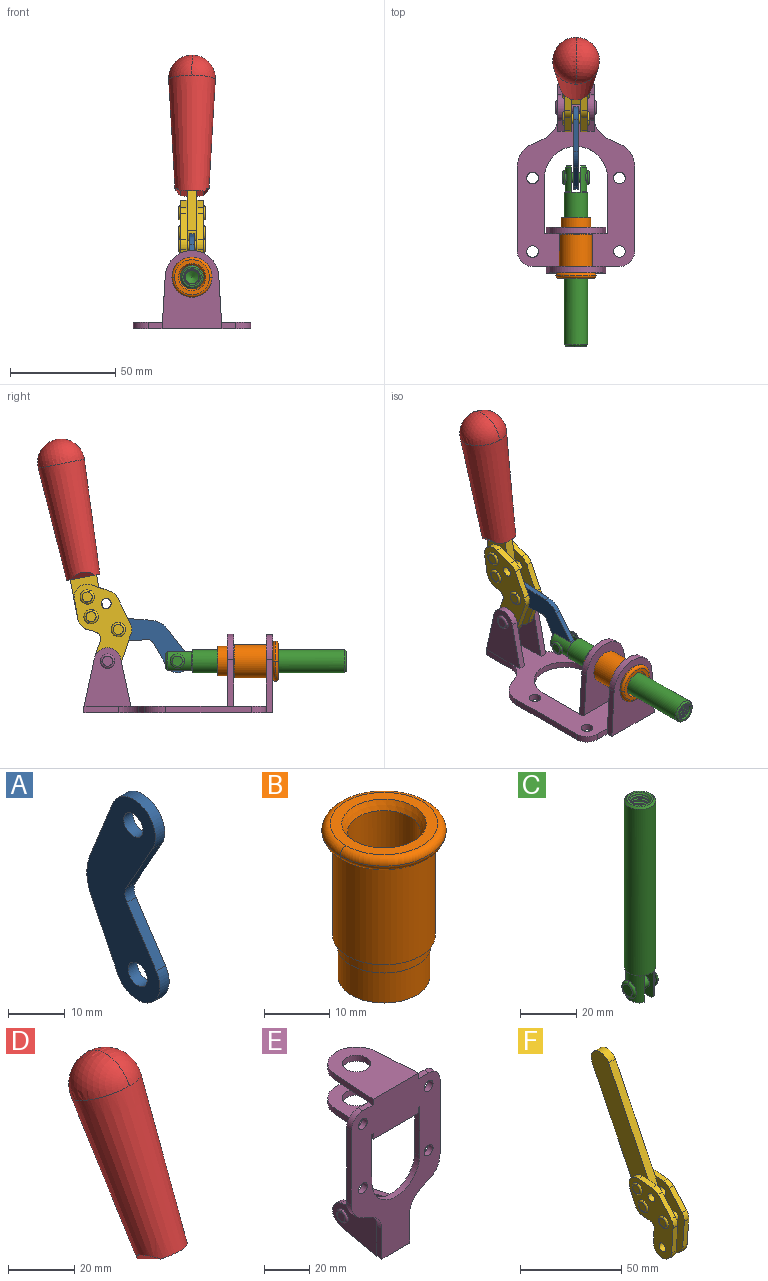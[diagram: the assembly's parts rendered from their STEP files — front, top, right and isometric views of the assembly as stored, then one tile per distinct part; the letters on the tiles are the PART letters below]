
ASSEMBLY  parts=6 mates=6
PART A: 12 faces, bbox 2.3x18.2x42.8 mm
  f0: cylinder r=2.4mm len=4.8mm, axis (1,0,0), area 34.9mm2, adj f4,f11
  f1: cylinder r=10.41mm len=8.47mm, axis (1,0,0), area 20.2mm2, adj f4,f9,f10,f11
  f2: cylinder r=3.05mm len=3.16mm, axis (1,0,0), area 7.7mm2, adj f4,f6,f7,f11
  f3: cylinder r=2.4mm len=4.8mm, axis (1,0,0), area 34.9mm2, adj f4,f11
  f4: plane 42.81x18.23mm, normal (-1,0,0), area 414.1mm2, adj f0,f1,f2,f3,f5,f6,f7,f8
  f5: cylinder r=5.54mm len=10.67mm, axis (1,0,0), area 41.8mm2, adj f4,f6,f10,f11
  f6: plane 11.66x6.53mm, normal (0,-0.87,-0.49), area 30.9mm2, adj f2,f4,f5,f11
  f7: plane 11.17x7.33mm, normal (0,-0.84,0.55), area 30.9mm2, adj f2,f4,f8,f11
  f8: cylinder r=5.54mm len=10.51mm, axis (1,0,0), area 41.8mm2, adj f4,f7,f9,f11
  f9: plane 13.67x6.67mm, normal (0,0.9,-0.44), area 35.1mm2, adj f1,f4,f8,f11
  f10: plane 14.1x5.7mm, normal (0,0.93,0.37), area 35.1mm2, adj f1,f4,f5,f11
  f11: plane 42.81x18.23mm, normal (1,0,0), area 414.1mm2, adj f0,f1,f2,f3,f5,f6,f7,f8
PART B: 15 faces, bbox 20.6x20.6x28.7 mm
  f0: torus R=8.26mm, axis (0,0,1), area 56.8mm2, adj f1,f10,f12
  f1: torus R=8.26mm, axis (0,0,1), area 56.8mm2, adj f0,f6,f13
  f2: cylinder r=5.59mm len=25.91mm, axis (0,0,1), area 909.6mm2, adj f3,f4
  f3: cone r=6.86mm half-angle=45deg, axis (0,0,-1), area 70.2mm2, adj f2,f14
  f4: cone r=6.47mm half-angle=30deg, axis (0,0,1), area 66.7mm2, adj f2,f13
  f5: cylinder r=7.04mm len=14.07mm, axis (0,0,1), area 252.6mm2, adj f11,f14
  f6: torus R=8.26mm, axis (0,0,1), area 56.8mm2, adj f1,f12,f13
  f7: cylinder r=7.16mm len=14.33mm, axis (0,0,1), area 91.5mm2, adj f9,f11
  f8: cylinder r=7.86mm len=18.42mm, axis (0,0,1), area 909.6mm2, adj f9,f10
  f9: plane 15.72x15.72mm, normal (0,0,-1), area 33mm2, adj f7,f8
  f10: plane 16.51x16.51mm, normal (0,0,-1), area 19.9mm2, adj f0,f8,f12
  f11: plane 14.33x14.33mm, normal (0,0,-1), area 5.7mm2, adj f5,f7
  f12: torus R=8.26mm, axis (0,0,1), area 56.8mm2, adj f0,f6,f10
  f13: plane 16.51x16.51mm, normal (0,0,1), area 82.7mm2, adj f1,f4,f6
  f14: plane 14.07x14.07mm, normal (0,0,-1), area 7.8mm2, adj f3,f5
PART C: 48 faces, bbox 12.6x11.1x86.1 mm
  f0: torus R=2.41mm, axis (-1,0,0), area 15mm2, adj f30,f32,f34
  f1: torus R=2.41mm, axis (-1,0,0), area 15mm2, adj f29,f31,f33
  f2: cylinder r=5.54mm len=72.39mm, axis (0,0,1), area 2518.5mm2, adj f3,f4,f42,f43
  f3: cone r=5.54mm half-angle=45deg, axis (0,0,1), area 7.6mm2, adj f2,f5,f41
  f4: cone r=5.54mm half-angle=45deg, axis (0,0,-1), area 34.9mm2, adj f2,f39
  f5: cylinder r=5.08mm len=11.48mm, axis (0,0,1), area 108.3mm2, adj f3,f7,f8,f41
  f6: cylinder r=2.41mm len=4.83mm, axis (-1,0,0), area 71.2mm2, adj f40,f41
  f7: cylinder r=2.41mm len=4.83mm, axis (-1,0,0), area 7.6mm2, adj f5,f34
  f8: cone r=5.08mm half-angle=45deg, axis (0,0,1), area 10.6mm2, adj f5,f37,f41
  f9: cone r=3.98mm half-angle=45deg, axis (0,0,1), area 17.6mm2, adj f27,f39,f45,f46,f47
  f10: cylinder r=2.41mm len=4.83mm, axis (-1,0,0), area 7.6mm2, adj f33,f38
  f11: cylinder r=3.2mm len=6.4mm, axis (0,0,1), area 78.4mm2, adj f12,f28,f44,f45,f47
  f12: cylinder r=3.2mm len=6.4mm, axis (0,0,1), area 10.5mm2, adj f11,f13,f45,f47
  f13: cylinder r=3.2mm len=6.4mm, axis (0,0,1), area 10.5mm2, adj f12,f14,f45,f47
  f14: cylinder r=3.2mm len=6.4mm, axis (0,0,1), area 10.5mm2, adj f13,f15,f45,f47
  f15: cylinder r=3.2mm len=6.4mm, axis (0,0,1), area 10.5mm2, adj f14,f16,f45,f47
  f16: cylinder r=3.2mm len=6.4mm, axis (0,0,1), area 10.5mm2, adj f15,f17,f45,f47
  f17: cylinder r=3.2mm len=6.4mm, axis (0,0,1), area 10.5mm2, adj f16,f18,f45,f47
  f18: cylinder r=3.2mm len=6.4mm, axis (0,0,1), area 10.5mm2, adj f17,f19,f45,f47
  f19: cylinder r=3.2mm len=6.4mm, axis (0,0,1), area 10.5mm2, adj f18,f20,f45,f47
  f20: cylinder r=3.2mm len=6.4mm, axis (0,0,1), area 10.5mm2, adj f19,f21,f45,f47
  f21: cylinder r=3.2mm len=6.4mm, axis (0,0,1), area 10.5mm2, adj f20,f22,f45,f47
  f22: cylinder r=3.2mm len=6.4mm, axis (0,0,1), area 10.5mm2, adj f21,f23,f45,f47
  f23: cylinder r=3.2mm len=6.4mm, axis (0,0,1), area 10.5mm2, adj f22,f24,f45,f47
  f24: cylinder r=3.2mm len=6.4mm, axis (0,0,1), area 10.5mm2, adj f23,f25,f45,f47
  f25: cylinder r=3.2mm len=6.4mm, axis (0,0,1), area 10.5mm2, adj f24,f26,f45,f47
  f26: cylinder r=3.2mm len=6.4mm, axis (0,0,1), area 10.5mm2, adj f25,f27,f45,f47
  f27: cylinder r=3.2mm len=6.4mm, axis (0,0,1), area 7.4mm2, adj f9,f26,f45,f47
  f28: cone r=3.2mm half-angle=60deg, axis (0,0,1), area 37.2mm2, adj f11
  f29: plane 4.83x4.83mm, normal (-1,0,0), area 18.3mm2, adj f1,f31
  f30: plane 4.83x4.83mm, normal (1,0,0), area 18.3mm2, adj f0,f32
  f31: torus R=2.41mm, axis (-1,0,0), area 15mm2, adj f1,f29,f33
  f32: torus R=2.41mm, axis (-1,0,0), area 15mm2, adj f0,f30,f34
  f33: plane 6.83x6.83mm, normal (1,0,0), area 18.3mm2, adj f1,f10,f31
  f34: plane 6.83x6.83mm, normal (-1,0,0), area 18.3mm2, adj f0,f7,f32
  f35: cone r=5.08mm half-angle=45deg, axis (0,0,1), area 10.6mm2, adj f36,f38,f40
  f36: plane 7.25x1.97mm, normal (0,0,-1), area 10mm2, adj f35,f40
  f37: plane 7.25x1.97mm, normal (0,0,-1), area 10mm2, adj f8,f41
  f38: cylinder r=5.08mm len=11.48mm, axis (0,0,1), area 108.3mm2, adj f10,f35,f40,f42
  f39: plane 9.55x9.55mm, normal (0,0,1), area 22mm2, adj f4,f9
  f40: plane 12.76x10.09mm, normal (1,0,0), area 95.7mm2, adj f6,f35,f36,f38,f42,f43
  f41: plane 12.76x10.09mm, normal (-1,0,0), area 95.7mm2, adj f3,f5,f6,f8,f37,f43
  f42: cone r=5.54mm half-angle=45deg, axis (0,0,1), area 7.6mm2, adj f2,f38,f40
  f43: plane 11.07x4.7mm, normal (0,0,-1), area 50.4mm2, adj f2,f40,f41
  f44: plane 0.89x0.62mm, normal (-1,0,0), area 0.3mm2, adj f11,f45,f46,f47
  f45: bspline ~24.8x7.63mm, area 266.6mm2, adj f9,f11,f12,f13,f14,f15,f16,f17
  f46: bspline ~24.87x7.63mm, area 73.6mm2, adj f9,f44,f45,f47
  f47: bspline ~24.98x7.63mm, area 272.5mm2, adj f9,f11,f12,f13,f14,f15,f16,f17
PART D: 11 faces, bbox 22.3x42.6x64.5 mm
  f0: sphere r=11.13mm, area 411.4mm2, adj f1,f8
  f1: cone r=11.11mm half-angle=3.3deg, axis (0,0.44,0.9), area 3251.8mm2, adj f0,f7,f8,f9,f10
  f2: cylinder r=6.16mm len=11.7mm, axis (1,0,0), area 89.5mm2, adj f3,f4,f5,f6
  f3: plane 60.23x36.75mm, normal (-1,0,0), area 763.6mm2, adj f2,f4,f6,f10
  f4: plane 51.37x25.05mm, normal (0,0.9,-0.44), area 264.2mm2, adj f2,f3,f5,f10
  f5: plane 60.23x36.75mm, normal (1,0,0), area 763.6mm2, adj f2,f4,f6,f10
  f6: plane 51.37x25.05mm, normal (0,-0.9,0.44), area 264.2mm2, adj f2,f3,f5,f10
  f7: plane 9.95x5.95mm, normal (0.71,-0.31,-0.64), area 25.8mm2, adj f1,f10
  f8: sphere r=11.13mm, area 411.4mm2, adj f0,f1
  f9: plane 9.95x5.95mm, normal (-0.71,-0.31,-0.64), area 25.8mm2, adj f1,f10
  f10: plane 14.27x11.38mm, normal (0,-0.44,-0.9), area 106.7mm2, adj f1,f3,f4,f5,f6,f7,f9
PART E: 55 faces, bbox 55.7x37.4x89.8 mm
  f0: torus R=2.41mm, axis (-1,0,0), area 15mm2, adj f11,f15,f25
  f1: torus R=2.41mm, axis (-1,0,0), area 15mm2, adj f10,f12,f22
  f2: cylinder r=2.78mm len=5.56mm, axis (0,-1,0), area 54.2mm2, adj f30,f54
  f3: cylinder r=14.99mm len=29.97mm, axis (0,-1,0), area 145.9mm2, adj f30,f49,f53,f54
  f4: cylinder r=2.78mm len=5.56mm, axis (0,-1,0), area 54.2mm2, adj f30,f54
  f5: cylinder r=2.78mm len=5.56mm, axis (0,-1,0), area 54.2mm2, adj f30,f54
  f6: cylinder r=2.78mm len=5.56mm, axis (0,-1,0), area 54.2mm2, adj f30,f54
  f7: cylinder r=6.35mm len=12.7mm, axis (0,0,1), area 123.6mm2, adj f27,f51
  f8: cylinder r=6.35mm len=12.7mm, axis (0,0,-1), area 124.7mm2, adj f21,f35
  f9: cylinder r=2.41mm len=11.18mm, axis (-1,0,0), area 169.4mm2, adj f16,f19
  f10: plane 4.83x4.83mm, normal (1,0,0), area 18.3mm2, adj f1,f12
  f11: plane 4.83x4.83mm, normal (-1,0,0), area 18.3mm2, adj f0,f15
  f12: torus R=2.41mm, axis (-1,0,0), area 15mm2, adj f1,f10,f22
  f13: cylinder r=6.35mm len=12.41mm, axis (1,0,0), area 53.4mm2, adj f18,f19,f22,f23
  f14: cylinder r=6.35mm len=12.41mm, axis (-1,0,0), area 53.4mm2, adj f16,f17,f24,f25
  f15: torus R=2.41mm, axis (-1,0,0), area 15mm2, adj f0,f11,f25
  f16: plane 27.86x22.35mm, normal (1,0,0), area 425.4mm2, adj f9,f14,f17,f24,f30
  f17: plane 22.86x4.97mm, normal (0,0.21,0.98), area 72.5mm2, adj f14,f16,f25,f30
  f18: plane 22.86x4.97mm, normal (0,0.21,0.98), area 72.5mm2, adj f13,f19,f22,f30
  f19: plane 27.86x22.35mm, normal (-1,0,0), area 425.4mm2, adj f9,f13,f18,f23,f30
  f20: cylinder r=12.7mm len=25.35mm, axis (0,0,-1), area 119.8mm2, adj f21,f34,f35,f36
  f21: plane 34.21x28.07mm, normal (0,0,-1), area 702.4mm2, adj f8,f20,f30,f34,f36
  f22: plane 27.96x22.45mm, normal (1,0,0), area 407.2mm2, adj f1,f12,f13,f18,f23,f30,f42,f43
  f23: plane 22.86x4.97mm, normal (0,0.21,-0.98), area 72.5mm2, adj f13,f19,f22,f44
  f24: plane 22.86x4.97mm, normal (0,0.21,-0.98), area 72.5mm2, adj f14,f16,f25,f44
  f25: plane 27.86x22.35mm, normal (-1,0,0), area 407.1mm2, adj f0,f14,f15,f17,f24,f30,f45,f46
  f26: plane 3.1x0.95mm, normal (0,0,-1), area 2.7mm2, adj f30,f49,f50,f54
  f27: plane 34.21x28.07mm, normal (0,0,1), area 702.4mm2, adj f7,f28,f30,f50,f52
  f28: cylinder r=12.7mm len=25.35mm, axis (0,0,1), area 118.8mm2, adj f27,f50,f51,f52
  f29: plane 3.1x0.95mm, normal (0,0,-1), area 2.7mm2, adj f30,f52,f53,f54
  f30: plane 86.54x55.63mm, normal (0,1,0), area 2362.9mm2, adj f2,f3,f4,f5,f6,f16,f17,f18
  f31: plane 40.56x3.1mm, normal (-1,0,0), area 125.7mm2, adj f30,f32,f48,f54
  f32: cylinder r=7.11mm len=7.11mm, axis (0,-1,0), area 34.6mm2, adj f30,f31,f33,f54
  f33: plane 6.67x3.1mm, normal (0,0,1), area 20.4mm2, adj f30,f32,f34,f54
  f34: plane 25.39x3.13mm, normal (-1,0.06,0), area 79.5mm2, adj f20,f21,f33,f35,f54
  f35: plane 37.31x28.45mm, normal (0,0,1), area 789.9mm2, adj f8,f20,f34,f36,f54
  f36: plane 25.39x3.13mm, normal (1,0.06,0), area 79.5mm2, adj f20,f21,f35,f37,f54
  f37: plane 6.67x3.1mm, normal (0,0,1), area 20.4mm2, adj f30,f36,f38,f54
  f38: cylinder r=7.11mm len=7.11mm, axis (0,-1,0), area 34.6mm2, adj f30,f37,f39,f54
  f39: plane 40.56x3.1mm, normal (1,0,0), area 125.7mm2, adj f30,f38,f40,f54
  f40: cylinder r=11.18mm len=10.16mm, axis (0,-1,0), area 39.5mm2, adj f30,f39,f41,f54
  f41: plane 6.09x3.1mm, normal (0.42,0,-0.91), area 20.8mm2, adj f30,f40,f42,f54
  f42: cylinder r=11.18mm len=9.41mm, axis (0,-1,0), area 37.2mm2, adj f22,f30,f41,f43,f54
  f43: plane 16.5x3.1mm, normal (1,0,0), area 51.1mm2, adj f22,f42,f44,f54
  f44: plane 17.37x3.1mm, normal (0,0,-1), area 53.8mm2, adj f23,f24,f30,f43,f45,f54
  f45: plane 16.5x3.1mm, normal (-1,0,0), area 51.1mm2, adj f25,f44,f46,f54
  f46: cylinder r=11.18mm len=9.41mm, axis (0,-1,0), area 37.2mm2, adj f25,f30,f45,f47,f54
  f47: plane 6.09x3.1mm, normal (-0.42,0,-0.91), area 20.8mm2, adj f30,f46,f48,f54
  f48: cylinder r=11.18mm len=10.16mm, axis (0,-1,0), area 39.5mm2, adj f30,f31,f47,f54
  f49: plane 26.54x3.1mm, normal (-1,0,0), area 82.3mm2, adj f3,f26,f30,f54
  f50: plane 25.39x3.1mm, normal (1,0.06,0), area 78.8mm2, adj f26,f27,f28,f51,f54
  f51: plane 37.31x28.45mm, normal (0,0,-1), area 789.9mm2, adj f7,f28,f50,f52,f54
  f52: plane 25.39x3.1mm, normal (-1,0.06,0), area 78.8mm2, adj f27,f28,f29,f51,f54
  f53: plane 26.54x3.1mm, normal (1,0,0), area 82.3mm2, adj f3,f29,f30,f54
  f54: plane 89.66x55.63mm, normal (0,-1,0), area 2678.5mm2, adj f2,f3,f4,f5,f6,f26,f29,f31
PART F: 59 faces, bbox 12.9x60.2x99.6 mm
  f0: torus R=2.39mm, axis (-1,0,0), area 14.9mm2, adj f20,f43,f51
  f1: torus R=2.39mm, axis (-1,0,0), area 14.9mm2, adj f19,f42,f51
  f2: torus R=2.39mm, axis (-1,0,0), area 14.9mm2, adj f18,f35,f51
  f3: torus R=2.39mm, axis (-1,0,0), area 14.9mm2, adj f14,f17,f23
  f4: torus R=2.39mm, axis (-1,0,0), area 14.9mm2, adj f13,f16,f23
  f5: torus R=2.39mm, axis (-1,0,0), area 14.9mm2, adj f12,f15,f23
  f6: cylinder r=2.39mm len=4.78mm, axis (1,0,0), area 46.5mm2, adj f48,f50,f51
  f7: cylinder r=2.39mm len=4.78mm, axis (1,0,0), area 46.5mm2, adj f50,f51
  f8: cylinder r=6.35mm len=12.68mm, axis (1,0,0), area 61.8mm2, adj f38,f39,f50,f51
  f9: cylinder r=2.39mm len=4.78mm, axis (-1,0,0), area 70.5mm2, adj f46,f50
  f10: cylinder r=2.39mm len=4.78mm, axis (-1,0,0), area 46.5mm2, adj f23,f45,f46
  f11: cylinder r=2.39mm len=4.78mm, axis (-1,0,0), area 46.5mm2, adj f23,f46
  f12: plane 4.78x4.78mm, normal (1,0,0), area 17.9mm2, adj f5,f15
  f13: plane 4.78x4.78mm, normal (1,0,0), area 17.9mm2, adj f4,f16
  f14: plane 4.78x4.78mm, normal (1,0,0), area 17.9mm2, adj f3,f17
  f15: torus R=2.39mm, axis (-1,0,0), area 14.9mm2, adj f5,f12,f23
  f16: torus R=2.39mm, axis (-1,0,0), area 14.9mm2, adj f4,f13,f23
  f17: torus R=2.39mm, axis (-1,0,0), area 14.9mm2, adj f3,f14,f23
  f18: plane 4.78x4.78mm, normal (-1,0,0), area 17.9mm2, adj f2,f35
  f19: plane 4.78x4.78mm, normal (-1,0,0), area 17.9mm2, adj f1,f42
  f20: plane 4.78x4.78mm, normal (-1,0,0), area 17.9mm2, adj f0,f43
  f21: plane 2.26x0.2mm, normal (1,0,0), area 0.2mm2, adj f31,f44
  f22: plane 2.26x0.2mm, normal (-1,0,0), area 0.2mm2, adj f41,f44
  f23: plane 39.37x30.77mm, normal (1,0,0), area 565.5mm2, adj f3,f4,f5,f10,f11,f15,f16,f17
  f24: cylinder r=6.1mm len=4.15mm, axis (-1,0,0), area 14.7mm2, adj f23,f25,f32,f46
  f25: plane 10.25x9.01mm, normal (0,-0.75,0.66), area 42.3mm2, adj f23,f24,f26,f46
  f26: cylinder r=6.35mm len=4.64mm, axis (-1,0,0), area 15.6mm2, adj f23,f25,f27,f46
  f27: plane 15.84x3.1mm, normal (0,-1,-0.07), area 49.2mm2, adj f23,f26,f28,f46
  f28: cylinder r=6.35mm len=12.68mm, axis (-1,0,0), area 61.8mm2, adj f23,f27,f29,f46
  f29: plane 8.11x3.1mm, normal (0,1,0.07), area 25.2mm2, adj f23,f28,f30,f46
  f30: cylinder r=3.05mm len=3.25mm, axis (-1,0,0), area 14.8mm2, adj f23,f29,f31,f46
  f31: plane 5.99x3.1mm, normal (0,0.07,-1), area 18.6mm2, adj f21,f23,f30,f44,f46
  f32: plane 9.5x3.1mm, normal (0,-0.07,1), area 29.5mm2, adj f23,f24,f33,f46,f47
  f33: cylinder r=6.1mm len=8.63mm, axis (-1,0,0), area 39.1mm2, adj f23,f32,f34,f47
  f34: plane 8.65x3.96mm, normal (0,0.91,-0.42), area 29.5mm2, adj f23,f33,f44,f47
  f35: torus R=2.39mm, axis (-1,0,0), area 14.9mm2, adj f2,f18,f51
  f36: plane 10.25x9.01mm, normal (0,-0.75,0.66), area 42.3mm2, adj f37,f49,f50,f51
  f37: cylinder r=6.35mm len=4.64mm, axis (1,0,0), area 15.6mm2, adj f36,f38,f50,f51
  f38: plane 15.84x3.1mm, normal (0,-1,-0.07), area 49.2mm2, adj f8,f37,f50,f51
  f39: plane 8.11x3.1mm, normal (0,1,0.07), area 25.2mm2, adj f8,f40,f50,f51
  f40: cylinder r=3.05mm len=3.25mm, axis (1,0,0), area 14.8mm2, adj f39,f41,f50,f51
  f41: plane 5.99x3.1mm, normal (0,0.07,-1), area 18.6mm2, adj f22,f40,f44,f50,f51
  f42: torus R=2.39mm, axis (-1,0,0), area 14.9mm2, adj f1,f19,f51
  f43: torus R=2.39mm, axis (-1,0,0), area 14.9mm2, adj f0,f20,f51
  f44: cylinder r=6.35mm len=12.12mm, axis (-1,0,0), area 128.9mm2, adj f21,f22,f23,f31,f34,f41,f46,f47
  f45: plane 2.65x1.35mm, normal (1,0,0), area 1mm2, adj f10,f55
  f46: plane 39.08x20.42mm, normal (-1,0,0), area 412.5mm2, adj f9,f10,f11,f24,f25,f26,f27,f28
  f47: plane 77.62x39.82mm, normal (1,0,0), area 850mm2, adj f32,f33,f34,f44,f53,f54,f55
  f48: plane 2.65x1.35mm, normal (-1,0,0), area 1mm2, adj f6,f55
  f49: cylinder r=6.1mm len=4.15mm, axis (1,0,0), area 14.7mm2, adj f36,f50,f51,f56
  f50: plane 39.08x20.42mm, normal (1,0,0), area 412.5mm2, adj f6,f7,f8,f9,f36,f37,f38,f39
  f51: plane 39.37x30.77mm, normal (-1,0,0), area 565.5mm2, adj f0,f1,f2,f6,f7,f8,f35,f36
  f52: plane 8.65x3.96mm, normal (0,0.91,-0.42), area 29.5mm2, adj f44,f51,f57,f58
  f53: plane 68.49x33.4mm, normal (0,0.9,-0.44), area 358.1mm2, adj f44,f47,f54,f58
  f54: cylinder r=6.35mm len=12.06mm, axis (1,0,0), area 93.7mm2, adj f47,f53,f55,f58
  f55: plane 68.49x33.4mm, normal (0,-0.9,0.44), area 358.1mm2, adj f44,f45,f46,f47,f48,f50,f54,f58
  f56: plane 9.5x3.1mm, normal (0,-0.07,1), area 29.5mm2, adj f49,f50,f51,f57,f58
  f57: cylinder r=6.1mm len=8.63mm, axis (1,0,0), area 39.1mm2, adj f51,f52,f56,f58
  f58: plane 77.62x39.82mm, normal (-1,0,0), area 850mm2, adj f44,f52,f53,f54,f55,f56,f57
PLACE A rot(axis=(1,0,0),120.2deg) t=(0,34.13,11.13)mm
PLACE B rot(axis=(1,0,0),90deg) t=(0,9.43,0)mm
PLACE C rot(axis=(1,0,0),90deg) t=(0,23.85,0)mm
PLACE D rot(axis=(1,0,0),15deg) t=(0,9.44,49.24)mm
PLACE E rot(axis=(1,0,0),90deg) t=(0,9.43,0)mm fixed
PLACE F rot(axis=(1,0,0),15deg) t=(0,9.44,49.24)mm
MATE fastened D.f2 <-> F.f54  axis (1,0,0) through (0,63.89,120.54)mm
MATE slider E.f7 <-> C.f2  axis (0,-1,0) through (0,-36.96,24.61)mm
MATE revolute A.f3 <-> F.f4  axis (1,0,0) through (0,36.35,39.62)mm
MATE revolute A.f5 <-> C.f6  axis (1,0,0) through (0,8.38,24.61)mm
MATE fastened B.f2 <-> E.f7  axis (0,1,0) through (0,-36.96,24.61)mm
MATE revolute F.f7 <-> E.f0  axis (-1,0,0) through (0,41.52,24.61)mm
